# Revit family: FP_Revit_18_HC90PCR1_Rangehood_90001871A
name_source: partatom
category: Specialty Equipment
revit_build: Autodesk Revit 2018 (Build: 20170223_1515(x64)
units: mm (PartAtom-declared; Revit-internal decimal feet)

## family parameters
Always vertical = Yes
Cut with Voids When Loaded = Yes
OmniClass Number = 23.40.40.00
OmniClass Title = Food Service Equipment and Furnishings
Part Type = Normal
Room Calculation Point = No
Round Connector Dimension = Use Diameter
Shared = No
Work Plane-Based = No

## types (4) — shared parameters
Chassis - Depth = 290 mm  [stored 0.951444 ft]
Chassis - Height = 298 mm  [stored 0.97769 ft]
Chassis - Width = 320 mm  [stored 1.04987 ft]
Connector Description - Electrical = 230 V, 50Hz
Connector Description - Extraction = 150mm rigid or  semi-rigid ducting, 780m³/hr
Description = 90cm Rangehood
Manufacturer = Fisher & Paykel Appliances
Material - Body = Fisher & Paykel - Stainless Steel
Material - Buttons and Dials = Fisher & Paykel - Steel, Chrome Plated
Product - Depth = 500 mm  [stored 1.64042 ft]
Product - Width = 898 mm  [stored 2.94619 ft]
URL = www.fisherpaykel.com

## per-type parameters (varying)
| type | Material - COLOUR CHANGE |
| HC90PCB1 | Fisher & Paykel - Black |
| HC90PCR1 | Fisher & Paykel - Red |
| HC90PCTX1 | Fisher & Paykel - Stainless Steel |
| HC90PCW1 | Fisher & Paykel - White |

note: column(s) folded — value = type name in every type: Model

note: [stored X ft] marks values corroborated as IEEE doubles in the binary element streams (Revit-internal decimal feet)

## geometry (parser evidence)
native form markers: Sweep x2
no freeform markers — native parametric forms only
